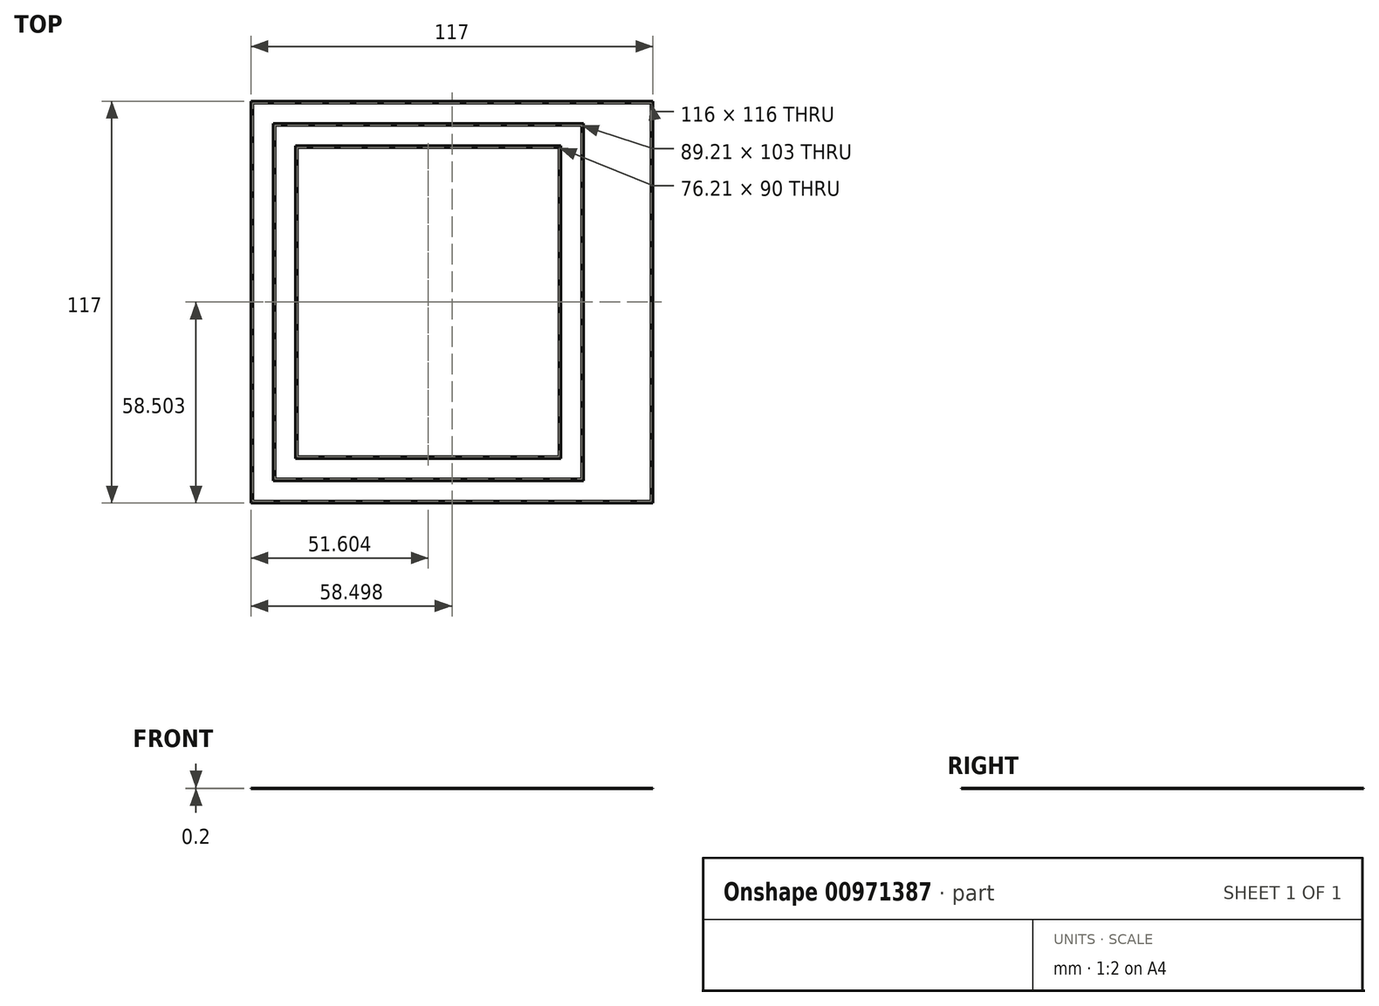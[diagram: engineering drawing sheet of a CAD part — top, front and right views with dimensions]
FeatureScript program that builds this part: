
annotation { "Feature Type Name" : "Feature", "Feature Type Description" : "" }
export const myFeature = defineFeature(function(context is Context, id is Id, definition is map)
    precondition{}
    {
        {
            assignVariable(context, id + "F0", {"name" : "LineHeight", "anyValue" : 0.2});
        }
        {
            var Q0;
            Q0=qCreatedBy(makeId("Top.planeOp"),FACE);
            var sketch = newSketch(context, id + "F1", { "sketchPlane" : qUnion([Q0])});
            skLineSegment(sketch, "E0.bottom", {"start": v(-91.48, 44.86) * mm, "end": v(25.52, 44.86) * mm});
            skLineSegment(sketch, "E0.top", {"start": v(-91.48, -72.14) * mm, "end": v(25.52, -72.14) * mm});
            skLineSegment(sketch, "E0.left", {"start": v(-91.48, 44.86) * mm, "end": v(-91.48, -72.14) * mm});
            skLineSegment(sketch, "E0.right", {"start": v(25.52, 44.86) * mm, "end": v(25.52, -72.14) * mm});
            skLineSegment(sketch, "E1.bottom", {"start": v(-84.98, 38.36) * mm, "end": v(5.23, 38.36) * mm});
            skLineSegment(sketch, "E1.top", {"start": v(-84.98, -65.64) * mm, "end": v(5.23, -65.64) * mm});
            skLineSegment(sketch, "E1.left", {"start": v(-84.98, 38.36) * mm, "end": v(-84.98, -65.64) * mm});
            skLineSegment(sketch, "E1.right", {"start": v(5.23, 38.36) * mm, "end": v(5.23, -65.64) * mm});
            skLineSegment(sketch, "E2.bottom", {"start": v(-78.48, 31.86) * mm, "end": v(-1.27, 31.86) * mm});
            skLineSegment(sketch, "E2.top", {"start": v(-78.48, -59.14) * mm, "end": v(-1.27, -59.14) * mm});
            skLineSegment(sketch, "E2.left", {"start": v(-78.48, 31.86) * mm, "end": v(-78.48, -59.14) * mm});
            skLineSegment(sketch, "E2.right", {"start": v(-1.27, 31.86) * mm, "end": v(-1.27, -59.14) * mm});
            skLineSegment(sketch, "E3", {"start": v(5.23, -58.64) * mm, "end": v(25.52, -58.64) * mm, "construction": true});
            skLineSegment(sketch, "E4", {"start": v(-90.98, 44.36) * mm, "end": v(25.02, 44.36) * mm});
            skLineSegment(sketch, "E5", {"start": v(25.02, 44.36) * mm, "end": v(25.02, -71.64) * mm});
            skLineSegment(sketch, "E6", {"start": v(25.02, -71.64) * mm, "end": v(-90.98, -71.64) * mm});
            skLineSegment(sketch, "E7", {"start": v(-90.98, -71.64) * mm, "end": v(-90.98, 44.36) * mm});
            skLineSegment(sketch, "E8", {"start": v(-84.48, 37.86) * mm, "end": v(4.73, 37.86) * mm});
            skLineSegment(sketch, "E9", {"start": v(4.73, 37.86) * mm, "end": v(4.73, -65.14) * mm});
            skLineSegment(sketch, "E10", {"start": v(4.73, -65.14) * mm, "end": v(-84.48, -65.14) * mm});
            skLineSegment(sketch, "E11", {"start": v(-84.48, -65.14) * mm, "end": v(-84.48, 37.86) * mm});
            skLineSegment(sketch, "E12", {"start": v(-77.98, 31.36) * mm, "end": v(-1.77, 31.36) * mm});
            skLineSegment(sketch, "E13", {"start": v(-1.77, 31.36) * mm, "end": v(-1.77, -58.64) * mm});
            skLineSegment(sketch, "E14", {"start": v(-1.77, -58.64) * mm, "end": v(-77.98, -58.64) * mm});
            skLineSegment(sketch, "E15", {"start": v(-77.98, -58.64) * mm, "end": v(-77.98, 31.36) * mm});
            skPoint(sketch, "E16.startSnap0", {"position": v(-85.51, 36.03) * mm});
            skSolve(sketch);
        }
        {
            var Q0;
            Q0=makeQuery(id+"F1.imprint","IMPRINT",FACE,{"disambiguationData":[TD([[makeQuery(id+"F1.imprint","IMPRINT",EDGE,{"derivedFrom":sQuery(id+"F1.wireOp",EDGE,"E0.bottom")}),-1.0]])]});
            var Q1;
            Q1=makeQuery(id+"F1.imprint","IMPRINT",FACE,{"disambiguationData":[TD([[makeQuery(id+"F1.imprint","IMPRINT",EDGE,{"derivedFrom":sQuery(id+"F1.wireOp",EDGE,"E1.bottom")}),-1.0]])]});
            var Q2;
            Q2=makeQuery(id+"F1.imprint","IMPRINT",FACE,{"disambiguationData":[TD([[makeQuery(id+"F1.imprint","IMPRINT",EDGE,{"derivedFrom":sQuery(id+"F1.wireOp",EDGE,"E2.bottom")}),-1.0]])]});
            var Q3;
            Q3=makeQuery(id+"F1.imprint","IMPRINT",FACE,{"disambiguationData":[TD([[makeQuery(id+"F1.imprint","IMPRINT",EDGE,{"derivedFrom":sQuery(id+"F1.wireOp",EDGE,"iO6pfZbY-7ntN-yKzr-tIri-R5R3f5lDf0fY")}),1.0]])]});
            var Q4;
            Q4=makeQuery(id+"F1.imprint","IMPRINT",FACE,{"disambiguationData":[TD([[makeQuery(id+"F1.imprint","IMPRINT",EDGE,{"derivedFrom":sQuery(id+"F1.wireOp",EDGE,"f7fcbfd7-52aa-416a-90d2-34237ff1b969.bottom")}),-1.0]])]});
            var Q5;
            Q5=makeQuery(id+"F1.imprint","IMPRINT",FACE,{"disambiguationData":[TD([[makeQuery(id+"F1.imprint","IMPRINT",EDGE,{"derivedFrom":sQuery(id+"F1.wireOp",EDGE,"HmofG7po-VB2C-NLRk-urQ5-j8slKDY0yj7J")}),1.0]])]});
            extrude(context, id + "F2", {"entities" : qUnion([Q0, Q1, Q2, Q3, Q4, Q5]), "depth" : (getVariable(context, 'LineHeight')) * mm, "offsetDistance" : 25 * mm});
        }
    });
